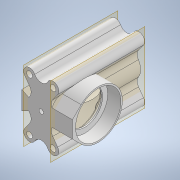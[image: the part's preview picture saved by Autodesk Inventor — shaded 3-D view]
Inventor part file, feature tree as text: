
AUTODESK INVENTOR PART (.ipt)
format: ipt  version: 2022 (Build 260153000, 153)  size: 463,360 bytes
history: native  units: mm
features: sketch x18, extrude x18, reference x11, other x6, plane x5, chamfer x3, projected_geometry x3, fillet x1, mirror x1
ambient origin geometry x8: Origin, YZ Plane, XZ Plane, XY Plane, X Axis, Y Axis, Z Axis, Center Point
bodies: Solid1 (feature_tree)
feature tree (66):
  sketch  "Sketch1"  dims[d0=0.3mm d1=2.0mm]
  plane  "Work Plane1"
  plane  "Work Plane6"
  extrude  "Extrusion1"  Depth=2.0mm
  extrude  "Extrusion2"  Depth=10.0mm TaperAngle=0.0deg
  extrude  "Extrusion3"  Depth=0.3mm TaperAngle=0.0deg
  extrude  "Extrusion4"  Depth=0.3mm TaperAngle=0.0deg
  extrude  "Extrusion5"  Depth=5.0mm
  fillet  "Fillet1"  Radius=4.0mm
  extrude  "Extrusion6"  Depth=10.0mm
  mirror  "Mirror1"
  extrude  "Extrusion7"  TaperAngle=0.0deg  [1 undecoded]
  chamfer  "Chamfer1"  Distance=7.3mm Angle=45.0deg
  plane  "Work Plane4"
  extrude  "Extrusion10"  TaperAngle=0.0deg  [1 undecoded]
  plane  "Work Plane5"
  extrude  "Extrusion11"  Depth=10.0mm TaperAngle=0.0deg
  extrude  "Extrusion12"  Depth=1.0mm TaperAngle=0.0deg
  chamfer  "Chamfer2"  Distance=1.0mm Angle=45.0deg
  extrude  "Extrusion13"  Depth=10.0mm TaperAngle=0.0deg
  extrude  "Extrusion16"  Depth=3.0mm TaperAngle=0.0deg
  extrude  "Extrusion18"  Depth=10.0mm
  extrude  "Extrusion19"  Depth=3.5mm
  extrude  "Extrusion21"  Depth=3.5mm TaperAngle=45.0deg
  extrude  "Extrusion22"  Depth=9.0mm TaperAngle=0.0deg
  chamfer  "Chamfer3"  Distance=9.0mm
  extrude  "Extrusion23"  Depth=0.872665mm
  extrude  "Extrusion24"  Depth=0.5mm
  reference  "Reference1"
  reference  "Reference2"
  reference  "Reference3"
  sketch  "Sketch2"  dims[d2=10.0mm d3=0.0mm d5=3.0mm d6=0.0mm]
  sketch  "Sketch3"  dims[d7=2.0mm d8=0.0mm d10=0.3mm d11=0.0mm]
  projected_geometry  "Projected Loop1"
  sketch  "Sketch5"  dims[d12=2.0mm d13=0.3mm d14=0.0mm]
  projected_geometry  "Projected Loop2"
  sketch  "Sketch6"  dims[d15=5.0mm d16=4.0mm d17=4.0mm]
  reference  "Reference6"
  reference  "Reference7"
  sketch  "Sketch7"  dims[d18=10.0mm d19=0.0mm d22=0.3mm]
  reference  "Reference8"
  reference  "Reference9"
  reference  "Reference10"
  reference  "Reference11"
  plane  "Work Plane2"
  other  "Work Point1"
  sketch  "Sketch9"  dims[d23=31.0mm d24=0.0mm d25=0.0mm d26=7.3mm d27=2.0mm d28=45.0deg]
  sketch  "Sketch12"  dims[d36=2.0mm d37=0.0mm d38=0.0mm]
  sketch  "Sketch13"  dims[d39=1.0mm d40=10.0mm d41=0.0mm]
  sketch  "Sketch14"  dims[d42=1.0mm d43=1.0mm d44=0.0mm d45=1.0mm d46=2.0mm d47=45.0deg]
  projected_geometry  "Projected Loop3"
  sketch  "Sketch15"  dims[d48=3.0mm d49=0.0mm d56=10.0mm d57=0.0mm]
  sketch  "Sketch19"  dims[d69=1.0mm d70=3.0mm d71=2.0mm d72=0.0mm d73=0.0mm]
  reference  "Reference13"
  sketch  "Sketch22"  dims[d74=10.0mm d75=0.0mm d79=3.0mm]
  sketch  "Sketch23"  dims[d80=0.0mm d81=0.0mm d82=3.5mm]
  sketch  "Sketch25"  dims[d83=1.0mm d84=0.0mm d85=3.5mm d86=2.0mm d87=45.0deg]
  reference  "Reference14"
  sketch  "Sketch26"  dims[d88=1.0mm d89=9.0mm d90=0.0mm]
  sketch  "Sketch27"  dims[d91=45.0deg d92=9.0mm d93=0.0mm]
  sketch  "Sketch28"  dims[d53=0.5mm d54=0.872665mm d55=0.5mm d67=0.5mm d68=0.872665mm d76=0.5mm d77=0.872665mm]
  other  "<userpath>\OneDrive - Imperial College London\ROBOICP MK2\solids feeder assembly.iam"
  other  "solids feeder assembly.iam"
  other  "shaft endcap:1"
  other  "Screw Shaft:1"
  other  "smol stepper:1"
note: 2 required parameter values undecoded (feature->parameter linkage not recoverable at this tier; creation-order binding heuristic only, values carry confidence <= 0.55)
